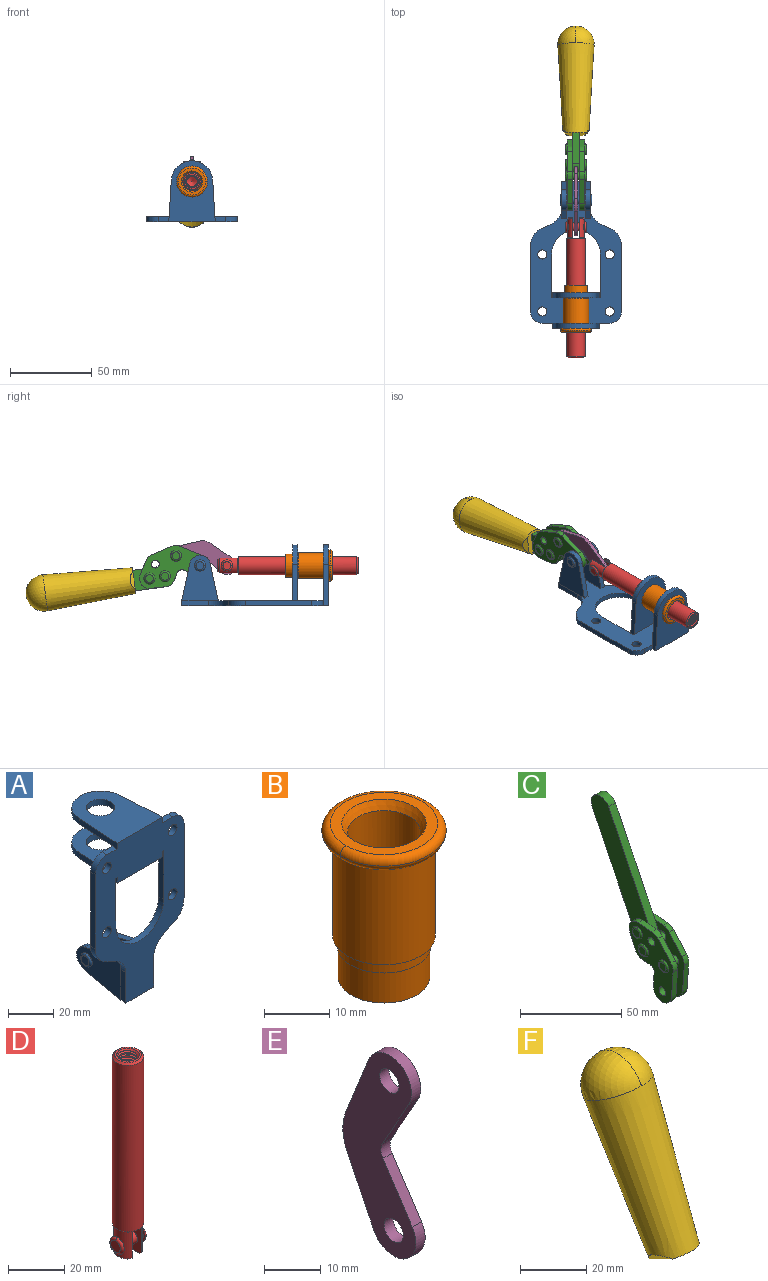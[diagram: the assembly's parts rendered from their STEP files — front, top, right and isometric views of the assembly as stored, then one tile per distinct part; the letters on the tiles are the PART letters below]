
ASSEMBLY  parts=6 mates=6
PART A: 55 faces, bbox 55.7x37.4x89.8 mm
  f0: torus R=2.41mm, axis (-1,0,0), area 15mm2, adj f11,f15,f25
  f1: torus R=2.41mm, axis (-1,0,0), area 15mm2, adj f10,f12,f22
  f2: cylinder r=2.78mm len=5.56mm, axis (0,-1,0), area 54.2mm2, adj f30,f54
  f3: cylinder r=14.99mm len=29.97mm, axis (0,-1,0), area 145.9mm2, adj f30,f49,f53,f54
  f4: cylinder r=2.78mm len=5.56mm, axis (0,-1,0), area 54.2mm2, adj f30,f54
  f5: cylinder r=2.78mm len=5.56mm, axis (0,-1,0), area 54.2mm2, adj f30,f54
  f6: cylinder r=2.78mm len=5.56mm, axis (0,-1,0), area 54.2mm2, adj f30,f54
  f7: cylinder r=6.35mm len=12.7mm, axis (0,0,1), area 123.6mm2, adj f27,f51
  f8: cylinder r=6.35mm len=12.7mm, axis (0,0,-1), area 124.7mm2, adj f21,f35
  f9: cylinder r=2.41mm len=11.18mm, axis (-1,0,0), area 169.4mm2, adj f16,f19
  f10: plane 4.83x4.83mm, normal (1,0,0), area 18.3mm2, adj f1,f12
  f11: plane 4.83x4.83mm, normal (-1,0,0), area 18.3mm2, adj f0,f15
  f12: torus R=2.41mm, axis (-1,0,0), area 15mm2, adj f1,f10,f22
  f13: cylinder r=6.35mm len=12.41mm, axis (1,0,0), area 53.4mm2, adj f18,f19,f22,f23
  f14: cylinder r=6.35mm len=12.41mm, axis (-1,0,0), area 53.4mm2, adj f16,f17,f24,f25
  f15: torus R=2.41mm, axis (-1,0,0), area 15mm2, adj f0,f11,f25
  f16: plane 27.86x22.35mm, normal (1,0,0), area 425.4mm2, adj f9,f14,f17,f24,f30
  f17: plane 22.86x4.97mm, normal (0,0.21,0.98), area 72.5mm2, adj f14,f16,f25,f30
  f18: plane 22.86x4.97mm, normal (0,0.21,0.98), area 72.5mm2, adj f13,f19,f22,f30
  f19: plane 27.86x22.35mm, normal (-1,0,0), area 425.4mm2, adj f9,f13,f18,f23,f30
  f20: cylinder r=12.7mm len=25.35mm, axis (0,0,-1), area 119.8mm2, adj f21,f34,f35,f36
  f21: plane 34.21x28.07mm, normal (0,0,-1), area 702.4mm2, adj f8,f20,f30,f34,f36
  f22: plane 27.96x22.45mm, normal (1,0,0), area 407.2mm2, adj f1,f12,f13,f18,f23,f30,f42,f43
  f23: plane 22.86x4.97mm, normal (0,0.21,-0.98), area 72.5mm2, adj f13,f19,f22,f44
  f24: plane 22.86x4.97mm, normal (0,0.21,-0.98), area 72.5mm2, adj f14,f16,f25,f44
  f25: plane 27.86x22.35mm, normal (-1,0,0), area 407.1mm2, adj f0,f14,f15,f17,f24,f30,f45,f46
  f26: plane 3.1x0.95mm, normal (0,0,-1), area 2.7mm2, adj f30,f49,f50,f54
  f27: plane 34.21x28.07mm, normal (0,0,1), area 702.4mm2, adj f7,f28,f30,f50,f52
  f28: cylinder r=12.7mm len=25.35mm, axis (0,0,1), area 118.8mm2, adj f27,f50,f51,f52
  f29: plane 3.1x0.95mm, normal (0,0,-1), area 2.7mm2, adj f30,f52,f53,f54
  f30: plane 86.54x55.63mm, normal (0,1,0), area 2362.9mm2, adj f2,f3,f4,f5,f6,f16,f17,f18
  f31: plane 40.56x3.1mm, normal (-1,0,0), area 125.7mm2, adj f30,f32,f48,f54
  f32: cylinder r=7.11mm len=7.11mm, axis (0,-1,0), area 34.6mm2, adj f30,f31,f33,f54
  f33: plane 6.67x3.1mm, normal (0,0,1), area 20.4mm2, adj f30,f32,f34,f54
  f34: plane 25.39x3.13mm, normal (-1,0.06,0), area 79.5mm2, adj f20,f21,f33,f35,f54
  f35: plane 37.31x28.45mm, normal (0,0,1), area 789.9mm2, adj f8,f20,f34,f36,f54
  f36: plane 25.39x3.13mm, normal (1,0.06,0), area 79.5mm2, adj f20,f21,f35,f37,f54
  f37: plane 6.67x3.1mm, normal (0,0,1), area 20.4mm2, adj f30,f36,f38,f54
  f38: cylinder r=7.11mm len=7.11mm, axis (0,-1,0), area 34.6mm2, adj f30,f37,f39,f54
  f39: plane 40.56x3.1mm, normal (1,0,0), area 125.7mm2, adj f30,f38,f40,f54
  f40: cylinder r=11.18mm len=10.16mm, axis (0,-1,0), area 39.5mm2, adj f30,f39,f41,f54
  f41: plane 6.09x3.1mm, normal (0.42,0,-0.91), area 20.8mm2, adj f30,f40,f42,f54
  f42: cylinder r=11.18mm len=9.41mm, axis (0,-1,0), area 37.2mm2, adj f22,f30,f41,f43,f54
  f43: plane 16.5x3.1mm, normal (1,0,0), area 51.1mm2, adj f22,f42,f44,f54
  f44: plane 17.37x3.1mm, normal (0,0,-1), area 53.8mm2, adj f23,f24,f30,f43,f45,f54
  f45: plane 16.5x3.1mm, normal (-1,0,0), area 51.1mm2, adj f25,f44,f46,f54
  f46: cylinder r=11.18mm len=9.41mm, axis (0,-1,0), area 37.2mm2, adj f25,f30,f45,f47,f54
  f47: plane 6.09x3.1mm, normal (-0.42,0,-0.91), area 20.8mm2, adj f30,f46,f48,f54
  f48: cylinder r=11.18mm len=10.16mm, axis (0,-1,0), area 39.5mm2, adj f30,f31,f47,f54
  f49: plane 26.54x3.1mm, normal (-1,0,0), area 82.3mm2, adj f3,f26,f30,f54
  f50: plane 25.39x3.1mm, normal (1,0.06,0), area 78.8mm2, adj f26,f27,f28,f51,f54
  f51: plane 37.31x28.45mm, normal (0,0,-1), area 789.9mm2, adj f7,f28,f50,f52,f54
  f52: plane 25.39x3.1mm, normal (-1,0.06,0), area 78.8mm2, adj f27,f28,f29,f51,f54
  f53: plane 26.54x3.1mm, normal (1,0,0), area 82.3mm2, adj f3,f29,f30,f54
  f54: plane 89.66x55.63mm, normal (0,-1,0), area 2678.5mm2, adj f2,f3,f4,f5,f6,f26,f29,f31
PART B: 15 faces, bbox 20.6x20.6x28.7 mm
  f0: torus R=8.26mm, axis (0,0,1), area 56.8mm2, adj f1,f10,f12
  f1: torus R=8.26mm, axis (0,0,1), area 56.8mm2, adj f0,f6,f13
  f2: cylinder r=5.59mm len=25.91mm, axis (0,0,1), area 909.6mm2, adj f3,f4
  f3: cone r=6.86mm half-angle=45deg, axis (0,0,-1), area 70.2mm2, adj f2,f14
  f4: cone r=6.47mm half-angle=30deg, axis (0,0,1), area 66.7mm2, adj f2,f13
  f5: cylinder r=7.04mm len=14.07mm, axis (0,0,1), area 252.6mm2, adj f11,f14
  f6: torus R=8.26mm, axis (0,0,1), area 56.8mm2, adj f1,f12,f13
  f7: cylinder r=7.16mm len=14.33mm, axis (0,0,1), area 91.5mm2, adj f9,f11
  f8: cylinder r=7.86mm len=18.42mm, axis (0,0,1), area 909.6mm2, adj f9,f10
  f9: plane 15.72x15.72mm, normal (0,0,-1), area 33mm2, adj f7,f8
  f10: plane 16.51x16.51mm, normal (0,0,-1), area 19.9mm2, adj f0,f8,f12
  f11: plane 14.33x14.33mm, normal (0,0,-1), area 5.7mm2, adj f5,f7
  f12: torus R=8.26mm, axis (0,0,1), area 56.8mm2, adj f0,f6,f10
  f13: plane 16.51x16.51mm, normal (0,0,1), area 82.7mm2, adj f1,f4,f6
  f14: plane 14.07x14.07mm, normal (0,0,-1), area 7.8mm2, adj f3,f5
PART C: 59 faces, bbox 12.9x60.2x99.6 mm
  f0: torus R=2.39mm, axis (-1,0,0), area 14.9mm2, adj f20,f43,f51
  f1: torus R=2.39mm, axis (-1,0,0), area 14.9mm2, adj f19,f42,f51
  f2: torus R=2.39mm, axis (-1,0,0), area 14.9mm2, adj f18,f35,f51
  f3: torus R=2.39mm, axis (-1,0,0), area 14.9mm2, adj f14,f17,f23
  f4: torus R=2.39mm, axis (-1,0,0), area 14.9mm2, adj f13,f16,f23
  f5: torus R=2.39mm, axis (-1,0,0), area 14.9mm2, adj f12,f15,f23
  f6: cylinder r=2.39mm len=4.78mm, axis (1,0,0), area 46.5mm2, adj f48,f50,f51
  f7: cylinder r=2.39mm len=4.78mm, axis (1,0,0), area 46.5mm2, adj f50,f51
  f8: cylinder r=6.35mm len=12.68mm, axis (1,0,0), area 61.8mm2, adj f38,f39,f50,f51
  f9: cylinder r=2.39mm len=4.78mm, axis (-1,0,0), area 70.5mm2, adj f46,f50
  f10: cylinder r=2.39mm len=4.78mm, axis (-1,0,0), area 46.5mm2, adj f23,f45,f46
  f11: cylinder r=2.39mm len=4.78mm, axis (-1,0,0), area 46.5mm2, adj f23,f46
  f12: plane 4.78x4.78mm, normal (1,0,0), area 17.9mm2, adj f5,f15
  f13: plane 4.78x4.78mm, normal (1,0,0), area 17.9mm2, adj f4,f16
  f14: plane 4.78x4.78mm, normal (1,0,0), area 17.9mm2, adj f3,f17
  f15: torus R=2.39mm, axis (-1,0,0), area 14.9mm2, adj f5,f12,f23
  f16: torus R=2.39mm, axis (-1,0,0), area 14.9mm2, adj f4,f13,f23
  f17: torus R=2.39mm, axis (-1,0,0), area 14.9mm2, adj f3,f14,f23
  f18: plane 4.78x4.78mm, normal (-1,0,0), area 17.9mm2, adj f2,f35
  f19: plane 4.78x4.78mm, normal (-1,0,0), area 17.9mm2, adj f1,f42
  f20: plane 4.78x4.78mm, normal (-1,0,0), area 17.9mm2, adj f0,f43
  f21: plane 2.26x0.2mm, normal (1,0,0), area 0.2mm2, adj f31,f44
  f22: plane 2.26x0.2mm, normal (-1,0,0), area 0.2mm2, adj f41,f44
  f23: plane 39.37x30.77mm, normal (1,0,0), area 565.5mm2, adj f3,f4,f5,f10,f11,f15,f16,f17
  f24: cylinder r=6.1mm len=4.15mm, axis (-1,0,0), area 14.7mm2, adj f23,f25,f32,f46
  f25: plane 10.25x9.01mm, normal (0,-0.75,0.66), area 42.3mm2, adj f23,f24,f26,f46
  f26: cylinder r=6.35mm len=4.64mm, axis (-1,0,0), area 15.6mm2, adj f23,f25,f27,f46
  f27: plane 15.84x3.1mm, normal (0,-1,-0.07), area 49.2mm2, adj f23,f26,f28,f46
  f28: cylinder r=6.35mm len=12.68mm, axis (-1,0,0), area 61.8mm2, adj f23,f27,f29,f46
  f29: plane 8.11x3.1mm, normal (0,1,0.07), area 25.2mm2, adj f23,f28,f30,f46
  f30: cylinder r=3.05mm len=3.25mm, axis (-1,0,0), area 14.8mm2, adj f23,f29,f31,f46
  f31: plane 5.99x3.1mm, normal (0,0.07,-1), area 18.6mm2, adj f21,f23,f30,f44,f46
  f32: plane 9.5x3.1mm, normal (0,-0.07,1), area 29.5mm2, adj f23,f24,f33,f46,f47
  f33: cylinder r=6.1mm len=8.63mm, axis (-1,0,0), area 39.1mm2, adj f23,f32,f34,f47
  f34: plane 8.65x3.96mm, normal (0,0.91,-0.42), area 29.5mm2, adj f23,f33,f44,f47
  f35: torus R=2.39mm, axis (-1,0,0), area 14.9mm2, adj f2,f18,f51
  f36: plane 10.25x9.01mm, normal (0,-0.75,0.66), area 42.3mm2, adj f37,f49,f50,f51
  f37: cylinder r=6.35mm len=4.64mm, axis (1,0,0), area 15.6mm2, adj f36,f38,f50,f51
  f38: plane 15.84x3.1mm, normal (0,-1,-0.07), area 49.2mm2, adj f8,f37,f50,f51
  f39: plane 8.11x3.1mm, normal (0,1,0.07), area 25.2mm2, adj f8,f40,f50,f51
  f40: cylinder r=3.05mm len=3.25mm, axis (1,0,0), area 14.8mm2, adj f39,f41,f50,f51
  f41: plane 5.99x3.1mm, normal (0,0.07,-1), area 18.6mm2, adj f22,f40,f44,f50,f51
  f42: torus R=2.39mm, axis (-1,0,0), area 14.9mm2, adj f1,f19,f51
  f43: torus R=2.39mm, axis (-1,0,0), area 14.9mm2, adj f0,f20,f51
  f44: cylinder r=6.35mm len=12.12mm, axis (-1,0,0), area 128.9mm2, adj f21,f22,f23,f31,f34,f41,f46,f47
  f45: plane 2.65x1.35mm, normal (1,0,0), area 1mm2, adj f10,f55
  f46: plane 39.08x20.42mm, normal (-1,0,0), area 412.5mm2, adj f9,f10,f11,f24,f25,f26,f27,f28
  f47: plane 77.62x39.82mm, normal (1,0,0), area 850mm2, adj f32,f33,f34,f44,f53,f54,f55
  f48: plane 2.65x1.35mm, normal (-1,0,0), area 1mm2, adj f6,f55
  f49: cylinder r=6.1mm len=4.15mm, axis (1,0,0), area 14.7mm2, adj f36,f50,f51,f56
  f50: plane 39.08x20.42mm, normal (1,0,0), area 412.5mm2, adj f6,f7,f8,f9,f36,f37,f38,f39
  f51: plane 39.37x30.77mm, normal (-1,0,0), area 565.5mm2, adj f0,f1,f2,f6,f7,f8,f35,f36
  f52: plane 8.65x3.96mm, normal (0,0.91,-0.42), area 29.5mm2, adj f44,f51,f57,f58
  f53: plane 68.49x33.4mm, normal (0,0.9,-0.44), area 358.1mm2, adj f44,f47,f54,f58
  f54: cylinder r=6.35mm len=12.06mm, axis (1,0,0), area 93.7mm2, adj f47,f53,f55,f58
  f55: plane 68.49x33.4mm, normal (0,-0.9,0.44), area 358.1mm2, adj f44,f45,f46,f47,f48,f50,f54,f58
  f56: plane 9.5x3.1mm, normal (0,-0.07,1), area 29.5mm2, adj f49,f50,f51,f57,f58
  f57: cylinder r=6.1mm len=8.63mm, axis (1,0,0), area 39.1mm2, adj f51,f52,f56,f58
  f58: plane 77.62x39.82mm, normal (-1,0,0), area 850mm2, adj f44,f52,f53,f54,f55,f56,f57
PART D: 48 faces, bbox 12.6x11.1x86.1 mm
  f0: torus R=2.41mm, axis (-1,0,0), area 15mm2, adj f30,f32,f34
  f1: torus R=2.41mm, axis (-1,0,0), area 15mm2, adj f29,f31,f33
  f2: cylinder r=5.54mm len=72.39mm, axis (0,0,1), area 2518.5mm2, adj f3,f4,f42,f43
  f3: cone r=5.54mm half-angle=45deg, axis (0,0,1), area 7.6mm2, adj f2,f5,f41
  f4: cone r=5.54mm half-angle=45deg, axis (0,0,-1), area 34.9mm2, adj f2,f39
  f5: cylinder r=5.08mm len=11.48mm, axis (0,0,1), area 108.3mm2, adj f3,f7,f8,f41
  f6: cylinder r=2.41mm len=4.83mm, axis (-1,0,0), area 71.2mm2, adj f40,f41
  f7: cylinder r=2.41mm len=4.83mm, axis (-1,0,0), area 7.6mm2, adj f5,f34
  f8: cone r=5.08mm half-angle=45deg, axis (0,0,1), area 10.6mm2, adj f5,f37,f41
  f9: cone r=3.98mm half-angle=45deg, axis (0,0,1), area 17.6mm2, adj f27,f39,f45,f46,f47
  f10: cylinder r=2.41mm len=4.83mm, axis (-1,0,0), area 7.6mm2, adj f33,f38
  f11: cylinder r=3.2mm len=6.4mm, axis (0,0,1), area 78.4mm2, adj f12,f28,f44,f45,f47
  f12: cylinder r=3.2mm len=6.4mm, axis (0,0,1), area 10.5mm2, adj f11,f13,f45,f47
  f13: cylinder r=3.2mm len=6.4mm, axis (0,0,1), area 10.5mm2, adj f12,f14,f45,f47
  f14: cylinder r=3.2mm len=6.4mm, axis (0,0,1), area 10.5mm2, adj f13,f15,f45,f47
  f15: cylinder r=3.2mm len=6.4mm, axis (0,0,1), area 10.5mm2, adj f14,f16,f45,f47
  f16: cylinder r=3.2mm len=6.4mm, axis (0,0,1), area 10.5mm2, adj f15,f17,f45,f47
  f17: cylinder r=3.2mm len=6.4mm, axis (0,0,1), area 10.5mm2, adj f16,f18,f45,f47
  f18: cylinder r=3.2mm len=6.4mm, axis (0,0,1), area 10.5mm2, adj f17,f19,f45,f47
  f19: cylinder r=3.2mm len=6.4mm, axis (0,0,1), area 10.5mm2, adj f18,f20,f45,f47
  f20: cylinder r=3.2mm len=6.4mm, axis (0,0,1), area 10.5mm2, adj f19,f21,f45,f47
  f21: cylinder r=3.2mm len=6.4mm, axis (0,0,1), area 10.5mm2, adj f20,f22,f45,f47
  f22: cylinder r=3.2mm len=6.4mm, axis (0,0,1), area 10.5mm2, adj f21,f23,f45,f47
  f23: cylinder r=3.2mm len=6.4mm, axis (0,0,1), area 10.5mm2, adj f22,f24,f45,f47
  f24: cylinder r=3.2mm len=6.4mm, axis (0,0,1), area 10.5mm2, adj f23,f25,f45,f47
  f25: cylinder r=3.2mm len=6.4mm, axis (0,0,1), area 10.5mm2, adj f24,f26,f45,f47
  f26: cylinder r=3.2mm len=6.4mm, axis (0,0,1), area 10.5mm2, adj f25,f27,f45,f47
  f27: cylinder r=3.2mm len=6.4mm, axis (0,0,1), area 7.4mm2, adj f9,f26,f45,f47
  f28: cone r=3.2mm half-angle=60deg, axis (0,0,1), area 37.2mm2, adj f11
  f29: plane 4.83x4.83mm, normal (-1,0,0), area 18.3mm2, adj f1,f31
  f30: plane 4.83x4.83mm, normal (1,0,0), area 18.3mm2, adj f0,f32
  f31: torus R=2.41mm, axis (-1,0,0), area 15mm2, adj f1,f29,f33
  f32: torus R=2.41mm, axis (-1,0,0), area 15mm2, adj f0,f30,f34
  f33: plane 6.83x6.83mm, normal (1,0,0), area 18.3mm2, adj f1,f10,f31
  f34: plane 6.83x6.83mm, normal (-1,0,0), area 18.3mm2, adj f0,f7,f32
  f35: cone r=5.08mm half-angle=45deg, axis (0,0,1), area 10.6mm2, adj f36,f38,f40
  f36: plane 7.25x1.97mm, normal (0,0,-1), area 10mm2, adj f35,f40
  f37: plane 7.25x1.97mm, normal (0,0,-1), area 10mm2, adj f8,f41
  f38: cylinder r=5.08mm len=11.48mm, axis (0,0,1), area 108.3mm2, adj f10,f35,f40,f42
  f39: plane 9.55x9.55mm, normal (0,0,1), area 22mm2, adj f4,f9
  f40: plane 12.76x10.09mm, normal (1,0,0), area 95.7mm2, adj f6,f35,f36,f38,f42,f43
  f41: plane 12.76x10.09mm, normal (-1,0,0), area 95.7mm2, adj f3,f5,f6,f8,f37,f43
  f42: cone r=5.54mm half-angle=45deg, axis (0,0,1), area 7.6mm2, adj f2,f38,f40
  f43: plane 11.07x4.7mm, normal (0,0,-1), area 50.4mm2, adj f2,f40,f41
  f44: plane 0.89x0.62mm, normal (-1,0,0), area 0.3mm2, adj f11,f45,f46,f47
  f45: bspline ~24.8x7.63mm, area 266.6mm2, adj f9,f11,f12,f13,f14,f15,f16,f17
  f46: bspline ~24.87x7.63mm, area 73.6mm2, adj f9,f44,f45,f47
  f47: bspline ~24.98x7.63mm, area 272.5mm2, adj f9,f11,f12,f13,f14,f15,f16,f17
PART E: 12 faces, bbox 2.3x18.2x42.8 mm
  f0: cylinder r=2.4mm len=4.8mm, axis (1,0,0), area 34.9mm2, adj f4,f11
  f1: cylinder r=10.41mm len=8.47mm, axis (1,0,0), area 20.2mm2, adj f4,f9,f10,f11
  f2: cylinder r=3.05mm len=3.16mm, axis (1,0,0), area 7.7mm2, adj f4,f6,f7,f11
  f3: cylinder r=2.4mm len=4.8mm, axis (1,0,0), area 34.9mm2, adj f4,f11
  f4: plane 42.81x18.23mm, normal (-1,0,0), area 414.1mm2, adj f0,f1,f2,f3,f5,f6,f7,f8
  f5: cylinder r=5.54mm len=10.67mm, axis (1,0,0), area 41.8mm2, adj f4,f6,f10,f11
  f6: plane 11.66x6.53mm, normal (0,-0.87,-0.49), area 30.9mm2, adj f2,f4,f5,f11
  f7: plane 11.17x7.33mm, normal (0,-0.84,0.55), area 30.9mm2, adj f2,f4,f8,f11
  f8: cylinder r=5.54mm len=10.51mm, axis (1,0,0), area 41.8mm2, adj f4,f7,f9,f11
  f9: plane 13.67x6.67mm, normal (0,0.9,-0.44), area 35.1mm2, adj f1,f4,f8,f11
  f10: plane 14.1x5.7mm, normal (0,0.93,0.37), area 35.1mm2, adj f1,f4,f5,f11
  f11: plane 42.81x18.23mm, normal (1,0,0), area 414.1mm2, adj f0,f1,f2,f3,f5,f6,f7,f8
PART F: 11 faces, bbox 22.3x42.6x64.5 mm
  f0: sphere r=11.13mm, area 411.4mm2, adj f1,f8
  f1: cone r=11.11mm half-angle=3.3deg, axis (0,0.44,0.9), area 3251.8mm2, adj f0,f7,f8,f9,f10
  f2: cylinder r=6.16mm len=11.7mm, axis (1,0,0), area 89.5mm2, adj f3,f4,f5,f6
  f3: plane 60.23x36.75mm, normal (-1,0,0), area 763.6mm2, adj f2,f4,f6,f10
  f4: plane 51.37x25.05mm, normal (0,0.9,-0.44), area 264.2mm2, adj f2,f3,f5,f10
  f5: plane 60.23x36.75mm, normal (1,0,0), area 763.6mm2, adj f2,f4,f6,f10
  f6: plane 51.37x25.05mm, normal (0,-0.9,0.44), area 264.2mm2, adj f2,f3,f5,f10
  f7: plane 9.95x5.95mm, normal (0.71,-0.31,-0.64), area 25.8mm2, adj f1,f10
  f8: sphere r=11.13mm, area 411.4mm2, adj f0,f1
  f9: plane 9.95x5.95mm, normal (-0.71,-0.31,-0.64), area 25.8mm2, adj f1,f10
  f10: plane 14.27x11.38mm, normal (0,-0.44,-0.9), area 106.7mm2, adj f1,f3,f4,f5,f6,f7,f9
PLACE A rot(axis=(1,0,0),90deg) t=(0,9.14,0)mm fixed
PLACE B rot(axis=(1,0,0),90deg) t=(0,9.14,0)mm
PLACE C rot(axis=(-1,0,0),71.8deg) t=(0,64.05,58)mm
PLACE D rot(axis=(1,0,0),90deg) t=(0,40.23,0)mm
PLACE E rot(axis=(1,0,0),102.9deg) t=(0,45.32,4.07)mm
PLACE F rot(axis=(-1,0,0),71.8deg) t=(-0.04,64.05,58)mm
MATE fastened F.f2 <-> C.f54  axis (1,0,0) through (-2.35,138.25,7.59)mm
MATE revolute D.f6 <-> E.f5  axis (-1,0,0) through (0,24.75,24.61)mm
MATE revolute C.f4 <-> E.f3  axis (-1,0,0) through (0,55.93,30.6)mm
MATE fastened B.f0 <-> A.f7  axis (0,1,0) through (0,-37.25,24.61)mm
MATE revolute A.f0 <-> C.f7  axis (-1,0,0) through (0,41.23,24.61)mm
MATE slider D.f2 <-> A.f7  axis (0,-1,0) through (0,-18.55,24.61)mm
